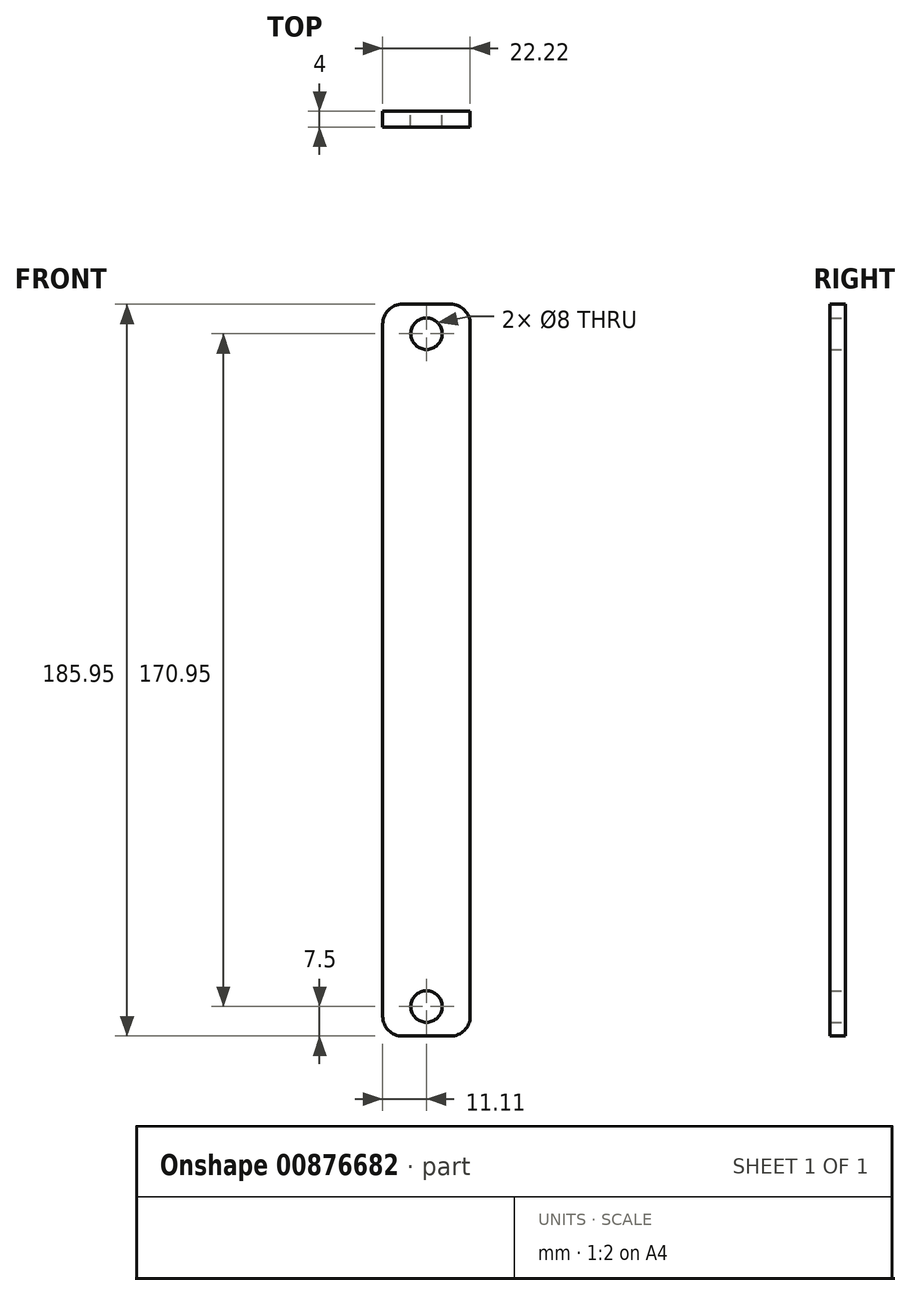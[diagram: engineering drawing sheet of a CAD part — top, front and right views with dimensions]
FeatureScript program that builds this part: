
annotation { "Feature Type Name" : "Feature", "Feature Type Description" : "" }
export const myFeature = defineFeature(function(context is Context, id is Id, definition is map)
    precondition{}
    {
        {
            var Q0;
            Q0=qCreatedBy(makeId("Front.planeOp"),FACE);
            var sketch = newSketch(context, id + "F0", { "sketchPlane" : qUnion([Q0])});
            skCircle(sketch, "E0", {"center": v(0, 0) * mm, "radius": 4 * mm});
            skCircle(sketch, "E1", {"center": v(0, 170.95) * mm, "radius": 4 * mm});
            skLineSegment(sketch, "E2.bottom", {"start": v(-11.1, 178.45) * mm, "end": v(11.1, 178.45) * mm});
            skLineSegment(sketch, "E2.top", {"start": v(-11.1, -7.5) * mm, "end": v(11.1, -7.5) * mm});
            skLineSegment(sketch, "E2.left", {"start": v(-11.1, 178.45) * mm, "end": v(-11.1, -7.5) * mm});
            skLineSegment(sketch, "E2.right", {"start": v(11.1, 178.45) * mm, "end": v(11.1, -7.5) * mm});
            skPoint(sketch, "E2.middle", {"position": v(0, 85.47) * mm});
            skSolve(sketch);
        }
        {
            var Q0;
            Q0 = qSketchRegion(id + "F0", true);
            extrude(context, id + "F1", {"entities" : qUnion([Q0]), "depth" : 4 * mm, "offsetDistance" : 25 * mm});
        }
        {
            var Q0;
            Q0=makeQuery(id+"F1.opExtrude","SWEPT_EDGE",EDGE,{"disambiguationData":[OSD([sQuery(id+"F0.wireOp",EDGE,"E2.top"),sQuery(id+"F0.wireOp",EDGE,"E2.left")])]});
            var Q1;
            Q1=makeQuery(id+"F1.opExtrude","SWEPT_EDGE",EDGE,{"disambiguationData":[OSD([sQuery(id+"F0.wireOp",EDGE,"E2.top"),sQuery(id+"F0.wireOp",EDGE,"E2.right")])]});
            var Q2;
            Q2=makeQuery(id+"F1.opExtrude","SWEPT_EDGE",EDGE,{"disambiguationData":[OSD([sQuery(id+"F0.wireOp",EDGE,"E2.bottom"),sQuery(id+"F0.wireOp",EDGE,"E2.right")])]});
            var Q3;
            Q3=makeQuery(id+"F1.opExtrude","SWEPT_EDGE",EDGE,{"disambiguationData":[OSD([sQuery(id+"F0.wireOp",EDGE,"E2.bottom"),sQuery(id+"F0.wireOp",EDGE,"E2.left")])]});
            fillet(context, id + "F2", {"entities" : qUnion([Q0, Q1, Q2, Q3]), "radius" : 5 * mm, "tangentPropagation" : true, "allowEdgeOverflow" : false});
        }
    });
